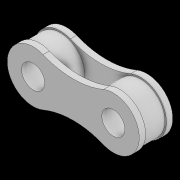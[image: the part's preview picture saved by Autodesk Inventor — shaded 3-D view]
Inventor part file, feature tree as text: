
AUTODESK INVENTOR PART (.ipt)
format: ipt  version: 2021 (Build 250183000, 183)  size: 134,144 bytes
history: native  units: in
note: dims shown in document units (in); Inventor stores cm internally (conversion verified against a paired STEP export)
features: extrude x2, sketch x2, plane x1, mirror x1
ambient origin geometry x8: Origin, YZ Plane, XZ Plane, XY Plane, X Axis, Y Axis, Z Axis, Center Point
bodies: Solid1 (feature_tree)
feature tree (6):
  plane  "Work Plane1"
  extrude  "Extrusion1"  Depth=0.1441in
  mirror  "Mirror1"
  extrude  "Extrusion2"  Depth=0.1299in
  sketch  "Sketch1"  dims[d1=0.3051in d2=0.1441in]
  sketch  "Sketch2"  dims[d0=0.065in d3=0.3228in d4=0.5in d5=0.4921in d6=0.1441in d7=0.0394in d8=0.0in d9=0.3051in d10=0.1299in d11=0.0in]
